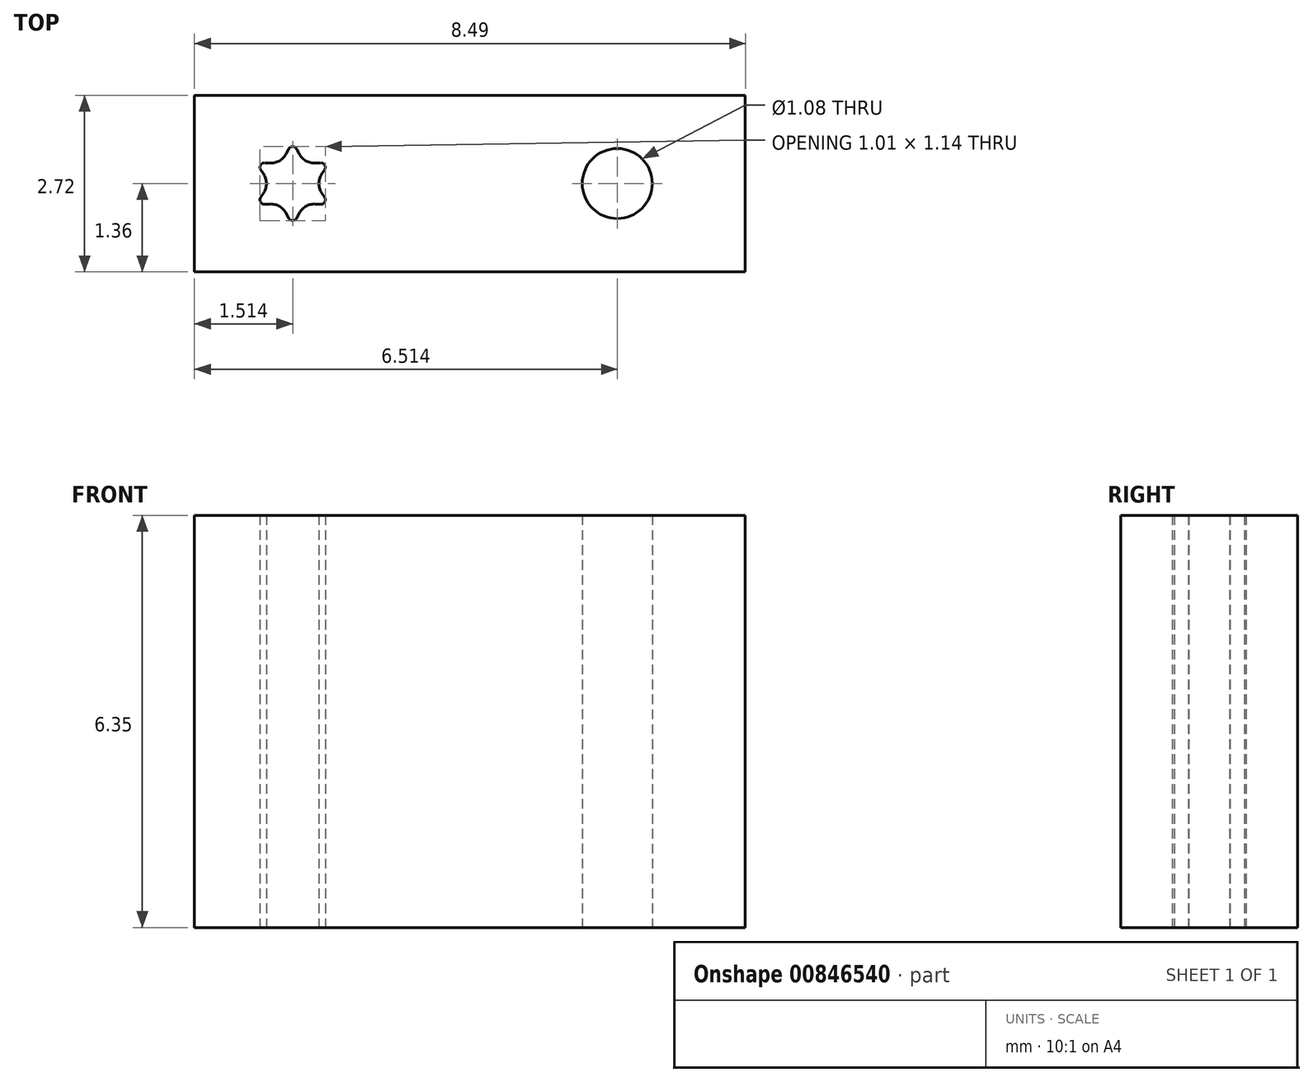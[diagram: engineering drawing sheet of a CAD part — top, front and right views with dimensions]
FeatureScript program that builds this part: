
annotation { "Feature Type Name" : "Feature", "Feature Type Description" : "" }
export const myFeature = defineFeature(function(context is Context, id is Id, definition is map)
    precondition{}
    {
        {
            var Q0;
            Q0=qCreatedBy(makeId("Top.planeOp"),FACE);
            var sketch = newSketch(context, id + "F0", { "sketchPlane" : qUnion([Q0])});
            skPoint(sketch, "E0", {"position": v(4.67, 0) * mm});
            skCircle(sketch, "E1", {"center": v(4.67, 0) * mm, "radius": 0.55 * mm});
            skCircle(sketch, "E2", {"center": v(4.67, 0) * mm, "radius": 0.38 * mm});
            skCircle(sketch, "E3", {"center": v(4.67, 0) * mm, "radius": 0.65 * mm});
            skLineSegment(sketch, "E4", {"start": v(4.67, 0) * mm, "end": v(4.67, 1.06) * mm, "construction": true});
            skLineSegment(sketch, "E5", {"start": v(4.67, 0) * mm, "end": v(4.3, 0.66) * mm, "construction": true});
            skPoint(sketch, "E6", {"position": v(4.35, 0.56) * mm});
            skArc(sketch, "E7", {"start": v(4.74, 0.5) * mm, "mid": v(4.67, 0.55) * mm, "end": v(4.6, 0.5) * mm});
            skLineSegment(sketch, "E8", {"start": v(4.6, 0.5) * mm, "end": v(4.59, 0.43) * mm});
            skLineSegment(sketch, "E9.MirrorCS", {"start": v(4.28, 0.3) * mm, "end": v(4.34, 0.3) * mm});
            skArc(sketch, "E10.trimOffspring", {"start": v(4.34, 0.3) * mm, "mid": v(4.48, 0.33) * mm, "end": v(4.59, 0.43) * mm});
            skArc(sketch, "E11.1.0", {"start": v(4.28, 0.3) * mm, "mid": v(4.2, 0.27) * mm, "end": v(4.2, 0.2) * mm});
            skLineSegment(sketch, "E11.1.1", {"start": v(4.2, 0.2) * mm, "end": v(4.25, 0.14) * mm});
            skArc(sketch, "E11.1.2", {"start": v(4.25, -0.14) * mm, "mid": v(4.3, 0) * mm, "end": v(4.25, 0.14) * mm});
            skLineSegment(sketch, "E11.1.3", {"start": v(4.2, -0.2) * mm, "end": v(4.25, -0.14) * mm});
            skArc(sketch, "E11.2.0", {"start": v(4.2, -0.2) * mm, "mid": v(4.2, -0.27) * mm, "end": v(4.28, -0.3) * mm});
            skLineSegment(sketch, "E11.2.1", {"start": v(4.28, -0.3) * mm, "end": v(4.34, -0.3) * mm});
            skArc(sketch, "E11.2.2", {"start": v(4.59, -0.43) * mm, "mid": v(4.48, -0.33) * mm, "end": v(4.34, -0.3) * mm});
            skLineSegment(sketch, "E11.2.3", {"start": v(4.6, -0.5) * mm, "end": v(4.59, -0.43) * mm});
            skArc(sketch, "E11.3.0", {"start": v(4.6, -0.5) * mm, "mid": v(4.67, -0.55) * mm, "end": v(4.74, -0.5) * mm});
            skLineSegment(sketch, "E11.3.1", {"start": v(4.74, -0.5) * mm, "end": v(4.76, -0.43) * mm});
            skArc(sketch, "E11.3.2", {"start": v(5, -0.3) * mm, "mid": v(4.86, -0.33) * mm, "end": v(4.76, -0.43) * mm});
            skLineSegment(sketch, "E11.3.3", {"start": v(5.07, -0.3) * mm, "end": v(5, -0.3) * mm});
            skArc(sketch, "E11.4.0", {"start": v(5.07, -0.3) * mm, "mid": v(5.15, -0.27) * mm, "end": v(5.14, -0.2) * mm});
            skLineSegment(sketch, "E11.4.1", {"start": v(5.14, -0.2) * mm, "end": v(5.1, -0.14) * mm});
            skArc(sketch, "E11.4.2", {"start": v(5.1, 0.14) * mm, "mid": v(5.05, 0) * mm, "end": v(5.1, -0.14) * mm});
            skLineSegment(sketch, "E11.4.3", {"start": v(5.14, 0.2) * mm, "end": v(5.1, 0.14) * mm});
            skArc(sketch, "E11.5.0", {"start": v(5.14, 0.2) * mm, "mid": v(5.15, 0.27) * mm, "end": v(5.07, 0.3) * mm});
            skLineSegment(sketch, "E11.5.1", {"start": v(5.07, 0.3) * mm, "end": v(5, 0.3) * mm});
            skArc(sketch, "E11.5.2", {"start": v(4.76, 0.43) * mm, "mid": v(4.86, 0.33) * mm, "end": v(5, 0.3) * mm});
            skLineSegment(sketch, "E11.5.3", {"start": v(4.74, 0.5) * mm, "end": v(4.76, 0.43) * mm});
            skLineSegment(sketch, "E12", {"start": v(4.67, 0) * mm, "end": v(9.66, 0) * mm, "construction": true});
            skCircle(sketch, "E13", {"center": v(9.66, 0) * mm, "radius": 0.54 * mm});
            skSolve(sketch);
        }
        {
            var Q0;
            Q0=qCreatedBy(makeId("Top.planeOp"),FACE);
            var sketch = newSketch(context, id + "F1", { "sketchPlane" : qUnion([Q0])});
            skLineSegment(sketch, "E14", {"start": v(4.67, 0) * mm, "end": v(4.67, -2) * mm, "construction": true});
            skCircle(sketch, "E15", {"center": v(4.67, -2) * mm, "radius": 0.4 * mm});
            skCircle(sketch, "E16", {"center": v(4.67, -2) * mm, "radius": 0.57 * mm});
            skCircle(sketch, "E17", {"center": v(4.67, -2) * mm, "radius": 0.68 * mm});
            skLineSegment(sketch, "E18", {"start": v(4.67, -2) * mm, "end": v(4.23, -1.23) * mm, "construction": true});
            skPoint(sketch, "E19", {"position": v(4.34, -1.42) * mm});
            skArc(sketch, "E20", {"start": v(4.32, -1.68) * mm, "mid": v(4.47, -1.65) * mm, "end": v(4.58, -1.54) * mm});
            skArc(sketch, "E21", {"start": v(4.67, -1.43) * mm, "mid": v(4.64, -1.44) * mm, "end": v(4.61, -1.47) * mm});
            skLineSegment(sketch, "E22", {"start": v(4.61, -1.47) * mm, "end": v(4.58, -1.54) * mm});
            skLineSegment(sketch, "E23.MirrorCS", {"start": v(4.25, -1.68) * mm, "end": v(4.32, -1.68) * mm});
            skArc(sketch, "E24.MirrorC", {"start": v(4.18, -1.71) * mm, "mid": v(4.2, -1.69) * mm, "end": v(4.25, -1.68) * mm});
            skArc(sketch, "E25.1.0", {"start": v(4.18, -1.71) * mm, "mid": v(4.17, -1.75) * mm, "end": v(4.18, -1.79) * mm});
            skLineSegment(sketch, "E25.1.1", {"start": v(4.18, -1.79) * mm, "end": v(4.22, -1.85) * mm});
            skArc(sketch, "E25.1.2", {"start": v(4.22, -2.15) * mm, "mid": v(4.27, -2) * mm, "end": v(4.22, -1.85) * mm});
            skLineSegment(sketch, "E25.1.3", {"start": v(4.18, -2.21) * mm, "end": v(4.22, -2.15) * mm});
            skArc(sketch, "E25.1.4", {"start": v(4.18, -2.28) * mm, "mid": v(4.17, -2.25) * mm, "end": v(4.18, -2.21) * mm});
            skArc(sketch, "E25.2.0", {"start": v(4.18, -2.28) * mm, "mid": v(4.2, -2.31) * mm, "end": v(4.25, -2.32) * mm});
            skLineSegment(sketch, "E25.2.1", {"start": v(4.25, -2.32) * mm, "end": v(4.32, -2.32) * mm});
            skArc(sketch, "E25.2.2", {"start": v(4.58, -2.46) * mm, "mid": v(4.47, -2.35) * mm, "end": v(4.32, -2.32) * mm});
            skLineSegment(sketch, "E25.2.3", {"start": v(4.61, -2.53) * mm, "end": v(4.58, -2.46) * mm});
            skArc(sketch, "E25.2.4", {"start": v(4.67, -2.57) * mm, "mid": v(4.64, -2.56) * mm, "end": v(4.61, -2.53) * mm});
            skArc(sketch, "E25.3.0", {"start": v(4.67, -2.57) * mm, "mid": v(4.71, -2.56) * mm, "end": v(4.74, -2.53) * mm});
            skLineSegment(sketch, "E25.3.1", {"start": v(4.74, -2.53) * mm, "end": v(4.77, -2.46) * mm});
            skArc(sketch, "E25.3.2", {"start": v(5.03, -2.32) * mm, "mid": v(4.88, -2.35) * mm, "end": v(4.77, -2.46) * mm});
            skLineSegment(sketch, "E25.3.3", {"start": v(5.1, -2.32) * mm, "end": v(5.03, -2.32) * mm});
            skArc(sketch, "E25.3.4", {"start": v(5.17, -2.29) * mm, "mid": v(5.14, -2.31) * mm, "end": v(5.1, -2.32) * mm});
            skArc(sketch, "E25.4.0", {"start": v(5.17, -2.29) * mm, "mid": v(5.18, -2.25) * mm, "end": v(5.16, -2.21) * mm});
            skLineSegment(sketch, "E25.4.1", {"start": v(5.16, -2.21) * mm, "end": v(5.12, -2.15) * mm});
            skArc(sketch, "E25.4.2", {"start": v(5.12, -1.85) * mm, "mid": v(5.08, -2) * mm, "end": v(5.12, -2.15) * mm});
            skLineSegment(sketch, "E25.4.3", {"start": v(5.16, -1.79) * mm, "end": v(5.12, -1.85) * mm});
            skArc(sketch, "E25.4.4", {"start": v(5.17, -1.72) * mm, "mid": v(5.18, -1.75) * mm, "end": v(5.16, -1.79) * mm});
            skArc(sketch, "E25.5.0", {"start": v(5.17, -1.72) * mm, "mid": v(5.14, -1.69) * mm, "end": v(5.1, -1.68) * mm});
            skLineSegment(sketch, "E25.5.1", {"start": v(5.1, -1.68) * mm, "end": v(5.03, -1.68) * mm});
            skArc(sketch, "E25.5.2", {"start": v(4.77, -1.54) * mm, "mid": v(4.88, -1.65) * mm, "end": v(5.03, -1.68) * mm});
            skLineSegment(sketch, "E25.5.3", {"start": v(4.74, -1.47) * mm, "end": v(4.77, -1.54) * mm});
            skArc(sketch, "E25.5.4", {"start": v(4.67, -1.43) * mm, "mid": v(4.71, -1.44) * mm, "end": v(4.74, -1.47) * mm});
            skLineSegment(sketch, "E26.bottom", {"start": v(3.16, -0.64) * mm, "end": v(11.65, -0.64) * mm});
            skLineSegment(sketch, "E26.top", {"start": v(3.16, -3.36) * mm, "end": v(11.65, -3.36) * mm});
            skLineSegment(sketch, "E26.left", {"start": v(3.16, -0.64) * mm, "end": v(3.16, -3.36) * mm});
            skLineSegment(sketch, "E26.right", {"start": v(11.65, -0.64) * mm, "end": v(11.65, -3.36) * mm});
            skCircle(sketch, "E27", {"center": v(9.67, -2) * mm, "radius": 0.54 * mm});
            skLineSegment(sketch, "E28", {"start": v(4.67, -2) * mm, "end": v(9.67, -2) * mm, "construction": true});
            skPoint(sketch, "E29", {"position": v(3.16, -2) * mm});
            skSolve(sketch);
        }
        {
            var Q0;
            Q0=makeQuery(id+"F1.imprint","IMPRINT",FACE,{"disambiguationData":[TD([[makeQuery(id+"F1.imprint","IMPRINT",EDGE,{"derivedFrom":sQuery(id+"F1.wireOp",EDGE,"E17")}),1.0]])]});
            var Q1;
            {var subQ4=sQuery(id+"F1.wireOp",EDGE,"E25.5.0");Q1=makeQuery(id+"F1.imprint","IMPRINT",FACE,{"disambiguationData":[TD([[makeQuery(id+"F1.imprint","IMPRINT",EDGE,{"derivedFrom":subQ4}),-1.0]])]});}
            var Q2;
            {var subQ4=sQuery(id+"F1.wireOp",EDGE,"E25.4.0");Q2=makeQuery(id+"F1.imprint","IMPRINT",FACE,{"disambiguationData":[TD([[makeQuery(id+"F1.imprint","IMPRINT",EDGE,{"derivedFrom":subQ4}),-1.0]])]});}
            var Q3;
            {var subQ0=sQuery(id+"F1.wireOp",EDGE,"E21");Q3=makeQuery(id+"F1.imprint","IMPRINT",FACE,{"disambiguationData":[TD([[makeQuery(id+"F1.imprint","IMPRINT",EDGE,{"derivedFrom":subQ0}),-1.0]])]});}
            var Q4;
            {var subQ4=sQuery(id+"F1.wireOp",EDGE,"E25.1.0");Q4=makeQuery(id+"F1.imprint","IMPRINT",FACE,{"disambiguationData":[TD([[makeQuery(id+"F1.imprint","IMPRINT",EDGE,{"derivedFrom":subQ4}),-1.0]])]});}
            var Q5;
            {var subQ4=sQuery(id+"F1.wireOp",EDGE,"E25.2.0");Q5=makeQuery(id+"F1.imprint","IMPRINT",FACE,{"disambiguationData":[TD([[makeQuery(id+"F1.imprint","IMPRINT",EDGE,{"derivedFrom":subQ4}),-1.0]])]});}
            var Q6;
            {var subQ4=sQuery(id+"F1.wireOp",EDGE,"E25.3.0");Q6=makeQuery(id+"F1.imprint","IMPRINT",FACE,{"disambiguationData":[TD([[makeQuery(id+"F1.imprint","IMPRINT",EDGE,{"derivedFrom":subQ4}),-1.0]])]});}
            var Q7;
            Q7=makeQuery(id+"F1.imprint","IMPRINT",FACE,{"disambiguationData":[TD([[makeQuery(id+"F1.imprint","IMPRINT",EDGE,{"derivedFrom":sQuery(id+"F1.wireOp",EDGE,"E17")}),-1.0]])]});
            extrude(context, id + "F2", {"entities" : qUnion([Q0, Q1, Q2, Q3, Q4, Q5, Q6, Q7]), "depth" : (0.25 * 25.4) * mm, "offsetDistance" : 25 * mm});
        }
    });
